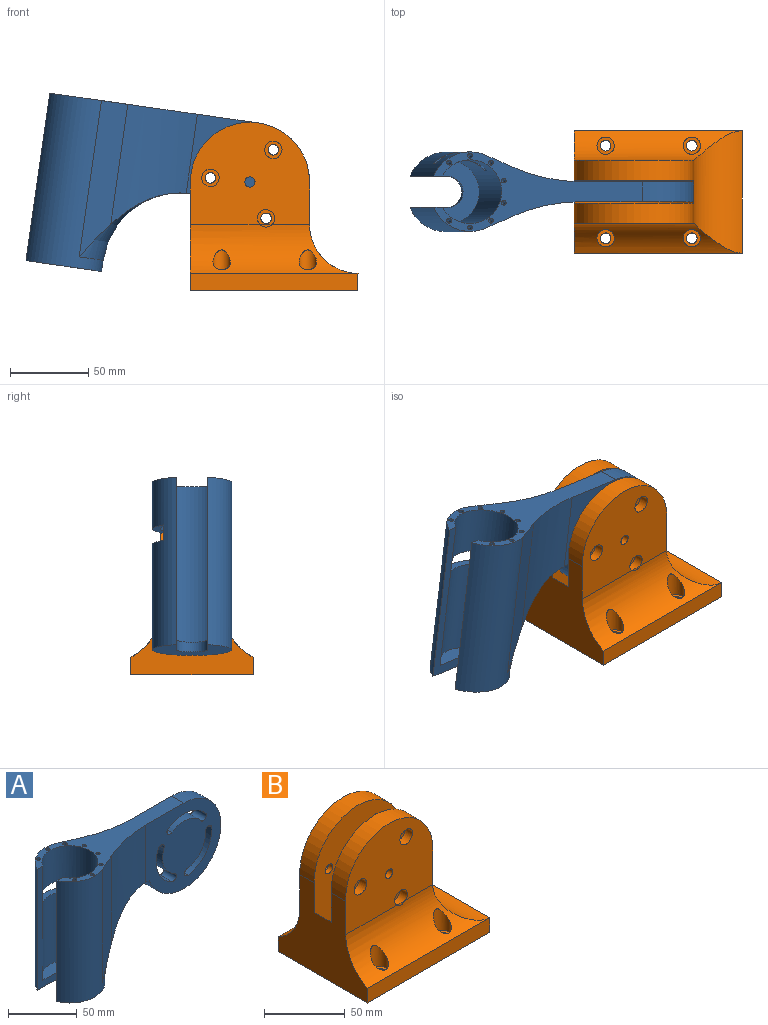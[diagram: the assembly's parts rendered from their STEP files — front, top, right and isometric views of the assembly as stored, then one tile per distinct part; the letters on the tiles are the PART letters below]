
ASSEMBLY  parts=2 mates=1
PART A: 50 faces, bbox 172.6x220.7x136.3 mm
  f0: cylinder r=25.4mm len=107.95mm, axis (0,0,-1), area 8735.3mm2, adj f2,f6,f8,f9,f10,f28,f45,f46
  f1: cylinder r=20.4mm len=101.6mm, axis (0,0,-1), area 10565.1mm2, adj f7,f8,f9,f10,f46,f47,f48,f49
  f2: cylinder r=1193.08mm len=100.8mm, axis (0,0,-1), area 1518.8mm2, adj f0,f8,f44,f45,f47,f48,f49
  f3: plane 1.43x0.11mm, normal (0,0,-1), area 0.1mm2, adj f5,f30,f45
  f4: plane 77.41x76.21mm, normal (0,1,0), area 4101.8mm2, adj f8,f29,f30,f31,f32,f33,f34,f35
  f5: plane 77.41x76.21mm, normal (0,-1,0), area 4101.8mm2, adj f3,f8,f30,f31,f32,f33,f34,f35
  f6: plane 50.8x48.75mm, normal (0,0,-1), area 1375.2mm2, adj f0,f9,f10,f11
  f7: plane 40.8x38.18mm, normal (0,0,1), area 759.3mm2, adj f1,f9,f10,f11
  f8: plane 134.51x50.8mm, normal (0,0,1), area 2058.3mm2, adj f0,f1,f2,f4,f5,f9,f10,f13
  f9: plane 107.95x23.35mm, normal (0,1,0), area 713.9mm2, adj f0,f1,f6,f7,f8,f11
  f10: plane 107.95x23.35mm, normal (0,-1,0), area 713.9mm2, adj f0,f1,f6,f7,f8,f11
  f11: cylinder r=10mm len=20mm, axis (0,0,1), area 199.5mm2, adj f6,f7,f9,f10
  f12: cone r=0mm half-angle=59deg, axis (0,0,1), area 8.2mm2, adj f13
  f13: cylinder r=1.5mm len=10mm, axis (0,0,1), area 94.2mm2, adj f8,f12
  f14: cone r=0mm half-angle=59deg, axis (0,0,1), area 8.2mm2, adj f15
  f15: cylinder r=1.5mm len=10mm, axis (0,0,1), area 94.2mm2, adj f8,f14
  f16: cone r=0mm half-angle=59deg, axis (0,0,1), area 8.2mm2, adj f17
  f17: cylinder r=1.5mm len=10mm, axis (0,0,1), area 94.2mm2, adj f8,f16
  f18: cone r=0mm half-angle=59deg, axis (0,0,1), area 8.2mm2, adj f19
  f19: cylinder r=1.5mm len=10mm, axis (0,0,1), area 94.2mm2, adj f8,f18
  f20: cone r=0mm half-angle=59deg, axis (0,0,1), area 8.2mm2, adj f21
  f21: cylinder r=1.5mm len=10mm, axis (0,0,1), area 94.2mm2, adj f8,f20
  f22: cone r=0mm half-angle=59deg, axis (0,0,1), area 8.2mm2, adj f23
  f23: cylinder r=1.5mm len=10mm, axis (0,0,1), area 94.2mm2, adj f8,f22
  f24: cone r=0mm half-angle=59deg, axis (0,0,1), area 8.2mm2, adj f25
  f25: cylinder r=1.5mm len=10mm, axis (0,0,1), area 94.2mm2, adj f8,f24
  f26: cone r=0mm half-angle=59deg, axis (0,0,1), area 8.2mm2, adj f27
  f27: cylinder r=1.5mm len=10mm, axis (0,0,1), area 94.2mm2, adj f8,f26
  f28: cylinder r=1193.08mm len=100.8mm, axis (0,0,-1), area 1640.4mm2, adj f0,f8,f43,f45
  f29: plane 1.43x0.11mm, normal (0,0,-1), area 0.1mm2, adj f4,f30,f45
  f30: cylinder r=38.1mm len=76.2mm, axis (0,1,0), area 2115.7mm2, adj f3,f4,f5,f8,f29,f45
  f31: cylinder r=3.25mm len=12.7mm, axis (0,1,0), area 129.7mm2, adj f4,f5,f32,f34
  f32: cylinder r=22.15mm len=23.56mm, axis (0,1,0), area 420.8mm2, adj f4,f5,f31,f33
  f33: cylinder r=3.25mm len=12.7mm, axis (0,1,0), area 129.7mm2, adj f4,f5,f32,f34
  f34: cylinder r=28.65mm len=30.47mm, axis (0,1,0), area 544.3mm2, adj f4,f5,f31,f33
  f35: cylinder r=3.25mm len=12.7mm, axis (0,1,0), area 129.7mm2, adj f4,f5,f36,f38
  f36: cylinder r=22.15mm len=28.05mm, axis (0,1,0), area 420.8mm2, adj f4,f5,f35,f37
  f37: cylinder r=3.25mm len=12.7mm, axis (0,1,0), area 129.7mm2, adj f4,f5,f36,f38
  f38: cylinder r=28.65mm len=36.28mm, axis (0,1,0), area 544.3mm2, adj f4,f5,f35,f37
  f39: cylinder r=3.25mm len=12.7mm, axis (0,1,0), area 129.7mm2, adj f4,f5,f40,f42
  f40: cylinder r=28.65mm len=38.54mm, axis (0,1,0), area 544.3mm2, adj f4,f5,f39,f41
  f41: cylinder r=3.25mm len=12.7mm, axis (0,1,0), area 129.7mm2, adj f4,f5,f40,f42
  f42: cylinder r=22.15mm len=29.8mm, axis (0,1,0), area 420.8mm2, adj f4,f5,f39,f41
  f43: cylinder r=110mm len=77.19mm, axis (0,0,-1), area 2772.4mm2, adj f5,f8,f28,f45
  f44: cylinder r=110mm len=77.19mm, axis (0,0,-1), area 2772.4mm2, adj f2,f4,f8,f45
  f45: torus R=75.4mm, axis (0,0,1), area 2153.8mm2, adj f0,f2,f3,f4,f5,f28,f29,f30
  f46: plane 10x3.54mm, normal (0.71,0.71,0), area 50mm2, adj f0,f1,f47,f48
  f47: plane 39.11x11.97mm, normal (0,0,1), area 197.7mm2, adj f0,f1,f2,f46,f49
  f48: plane 39.11x11.97mm, normal (0,0,-1), area 197.7mm2, adj f0,f1,f2,f46,f49
  f49: plane 10x5.8mm, normal (-0.66,0.75,0), area 77mm2, adj f1,f2,f47,f48
PART B: 64 faces, bbox 107.1x78.1x107.5 mm
  f0: cylinder r=35mm len=107.06mm, axis (1,0,0), area 2943.5mm2, adj f4,f5,f6,f8,f37,f46,f49,f52
  f1: cylinder r=35mm len=107.06mm, axis (1,0,0), area 2931.5mm2, adj f3,f5,f7,f8,f22,f23,f37,f40
  f2: plane 107.06x78.1mm, normal (0,0,-1), area 8217.7mm2, adj f3,f4,f5,f38,f39,f42,f45,f48
  f3: plane 107.06x11.06mm, normal (0,1,0), area 1184.4mm2, adj f1,f2,f5,f38
  f4: plane 107.06x11.06mm, normal (0,-1,0), area 1184.4mm2, adj f0,f2,f5,f38
  f5: plane 78.1x67.57mm, normal (-1,0,0), area 3142.4mm2, adj f0,f1,f2,f3,f4,f6,f7,f9
  f6: plane 76.2x65.33mm, normal (0,-1,0), area 4036.8mm2, adj f0,f5,f8,f33,f35,f51,f55,f58
  f7: plane 76.2x65.33mm, normal (0,1,0), area 4004.3mm2, adj f1,f5,f8,f9,f11,f12,f13,f14
  f8: plane 40.1x25.38mm, normal (1,0,0), area 691.9mm2, adj f0,f1,f6,f7,f9,f10,f33,f34
  f9: cylinder r=38.1mm len=76.2mm, axis (0,-1,0), area 1567.3mm2, adj f5,f7,f8,f10
  f10: plane 83.1x76.2mm, normal (0,-1,0), area 5094.3mm2, adj f5,f8,f9,f11,f36,f61,f62,f63
  f11: cylinder r=3.25mm len=12.7mm, axis (0,1,0), area 259.3mm2, adj f7,f10
  f12: plane 9x6.43mm, normal (-0.99,0,0.1), area 58.2mm2, adj f7,f13,f17,f18
  f13: plane 9x5.91mm, normal (-0.41,0,0.91), area 58.2mm2, adj f7,f12,f14,f18
  f14: plane 9x5.23mm, normal (0.59,0,0.81), area 58.2mm2, adj f7,f13,f15,f18
  f15: plane 9x6.43mm, normal (0.99,0,-0.1), area 58.2mm2, adj f7,f14,f16,f18
  f16: plane 9x5.91mm, normal (0.41,0,-0.91), area 58.2mm2, adj f7,f15,f17,f18
  f17: plane 9x5.23mm, normal (-0.59,0,-0.81), area 58.2mm2, adj f7,f12,f16,f18
  f18: plane 12.86x11.81mm, normal (0,1,0), area 72.8mm2, adj f12,f13,f14,f15,f16,f17,f63
  f19: plane 9x5.91mm, normal (0.41,0,-0.91), area 58.2mm2, adj f7,f20,f24,f25
  f20: plane 9x5.23mm, normal (-0.59,0,-0.81), area 58.2mm2, adj f7,f19,f21,f25
  f21: plane 9x6.43mm, normal (-0.99,0,0.1), area 58.2mm2, adj f7,f20,f22,f25
  f22: plane 9.09x5.91mm, normal (-0.41,0,0.91), area 58.4mm2, adj f1,f7,f21,f23,f25
  f23: plane 9.08x5.23mm, normal (0.59,0,0.81), area 58.3mm2, adj f1,f7,f22,f24,f25
  f24: plane 9x6.43mm, normal (0.99,0,-0.1), area 58.2mm2, adj f7,f19,f23,f25
  f25: plane 12.86x11.81mm, normal (0,1,0), area 72.8mm2, adj f19,f20,f21,f22,f23,f24,f62
  f26: plane 9x5.23mm, normal (0.59,0,0.81), area 58.2mm2, adj f7,f27,f31,f32
  f27: plane 9x6.43mm, normal (0.99,0,-0.1), area 58.2mm2, adj f7,f26,f28,f32
  f28: plane 9x5.91mm, normal (0.41,0,-0.91), area 58.2mm2, adj f7,f27,f29,f32
  f29: plane 9x5.23mm, normal (-0.59,0,-0.81), area 58.2mm2, adj f7,f28,f30,f32
  f30: plane 9x6.43mm, normal (-0.99,0,0.1), area 58.2mm2, adj f7,f29,f31,f32
  f31: plane 9x5.91mm, normal (-0.41,0,0.91), area 58.2mm2, adj f7,f26,f30,f32
  f32: plane 12.86x11.81mm, normal (0,1,0), area 72.8mm2, adj f26,f27,f28,f29,f30,f31,f61
  f33: cylinder r=38.1mm len=76.2mm, axis (0,1,0), area 1567.3mm2, adj f5,f6,f8,f34
  f34: plane 83.1x76.2mm, normal (0,1,0), area 5094.3mm2, adj f5,f8,f33,f35,f36,f54,f57,f60
  f35: cylinder r=3.25mm len=12.7mm, axis (0,-1,0), area 259.3mm2, adj f6,f34
  f36: cylinder r=45mm len=76.11mm, axis (0,1,0), area 1333.3mm2, adj f5,f8,f10,f34
  f37: cylinder r=31.12mm len=78.1mm, axis (0,-1,0), area 2787.6mm2, adj f0,f1,f8,f38
  f38: plane 78.1x11.06mm, normal (1,0,0), area 864.1mm2, adj f2,f3,f4,f37
  f39: cylinder r=3.38mm len=9mm, axis (0,0,1), area 191mm2, adj f2,f41
  f40: cylinder r=5.56mm len=17.05mm, axis (0,0,1), area 347.6mm2, adj f1,f41
  f41: plane 11.11x11.11mm, normal (0,0,1), area 61.1mm2, adj f39,f40
  f42: cylinder r=3.38mm len=9mm, axis (0,0,1), area 191mm2, adj f2,f44
  f43: cylinder r=5.56mm len=17.05mm, axis (0,0,1), area 347.6mm2, adj f1,f44
  f44: plane 11.11x11.11mm, normal (0,0,1), area 61.1mm2, adj f42,f43
  f45: cylinder r=3.38mm len=9mm, axis (0,0,1), area 191mm2, adj f2,f47
  f46: cylinder r=5.56mm len=17.05mm, axis (0,0,1), area 347.7mm2, adj f0,f47
  f47: plane 11.11x11.11mm, normal (0,0,1), area 61.1mm2, adj f45,f46
  f48: cylinder r=3.38mm len=9mm, axis (0,0,1), area 191mm2, adj f2,f50
  f49: cylinder r=5.56mm len=17.05mm, axis (0,0,1), area 347.7mm2, adj f0,f50
  f50: plane 11.11x11.11mm, normal (0,0,1), area 61.1mm2, adj f48,f49
  f51: cylinder r=5.56mm len=11.11mm, axis (0,-1,0), area 221.7mm2, adj f6,f52,f53
  f52: plane 7.65x1.53mm, normal (0,1,0), area 8mm2, adj f0,f51
  f53: plane 11.11x11.11mm, normal (0,-1,0), area 61.1mm2, adj f51,f54
  f54: cylinder r=3.38mm len=6.76mm, axis (0,-1,0), area 134.8mm2, adj f34,f53
  f55: cylinder r=5.56mm len=11.11mm, axis (0,-1,0), area 221.7mm2, adj f6,f56
  f56: plane 11.11x11.11mm, normal (0,-1,0), area 61.1mm2, adj f55,f57
  f57: cylinder r=3.38mm len=6.76mm, axis (0,-1,0), area 134.8mm2, adj f34,f56
  f58: cylinder r=5.56mm len=11.11mm, axis (0,-1,0), area 221.7mm2, adj f6,f59
  f59: plane 11.11x11.11mm, normal (0,-1,0), area 61.1mm2, adj f58,f60
  f60: cylinder r=3.38mm len=6.76mm, axis (0,-1,0), area 134.8mm2, adj f34,f59
  f61: cylinder r=3.38mm len=6.76mm, axis (0,-1,0), area 78.5mm2, adj f10,f32
  f62: cylinder r=3.38mm len=6.76mm, axis (0,-1,0), area 78.5mm2, adj f10,f25
  f63: cylinder r=3.38mm len=6.76mm, axis (0,-1,0), area 78.5mm2, adj f10,f18
PLACE A rot(axis=(0,1,0),8.1deg) t=(-36.7,-79.21,-7.84)mm
PLACE B t=(-28.87,-79.21,-24.11)mm fixed
MATE revolute A.f32 <-> B.f11  axis (0,-1,0) through (82.29,-85.56,39.39)mm
